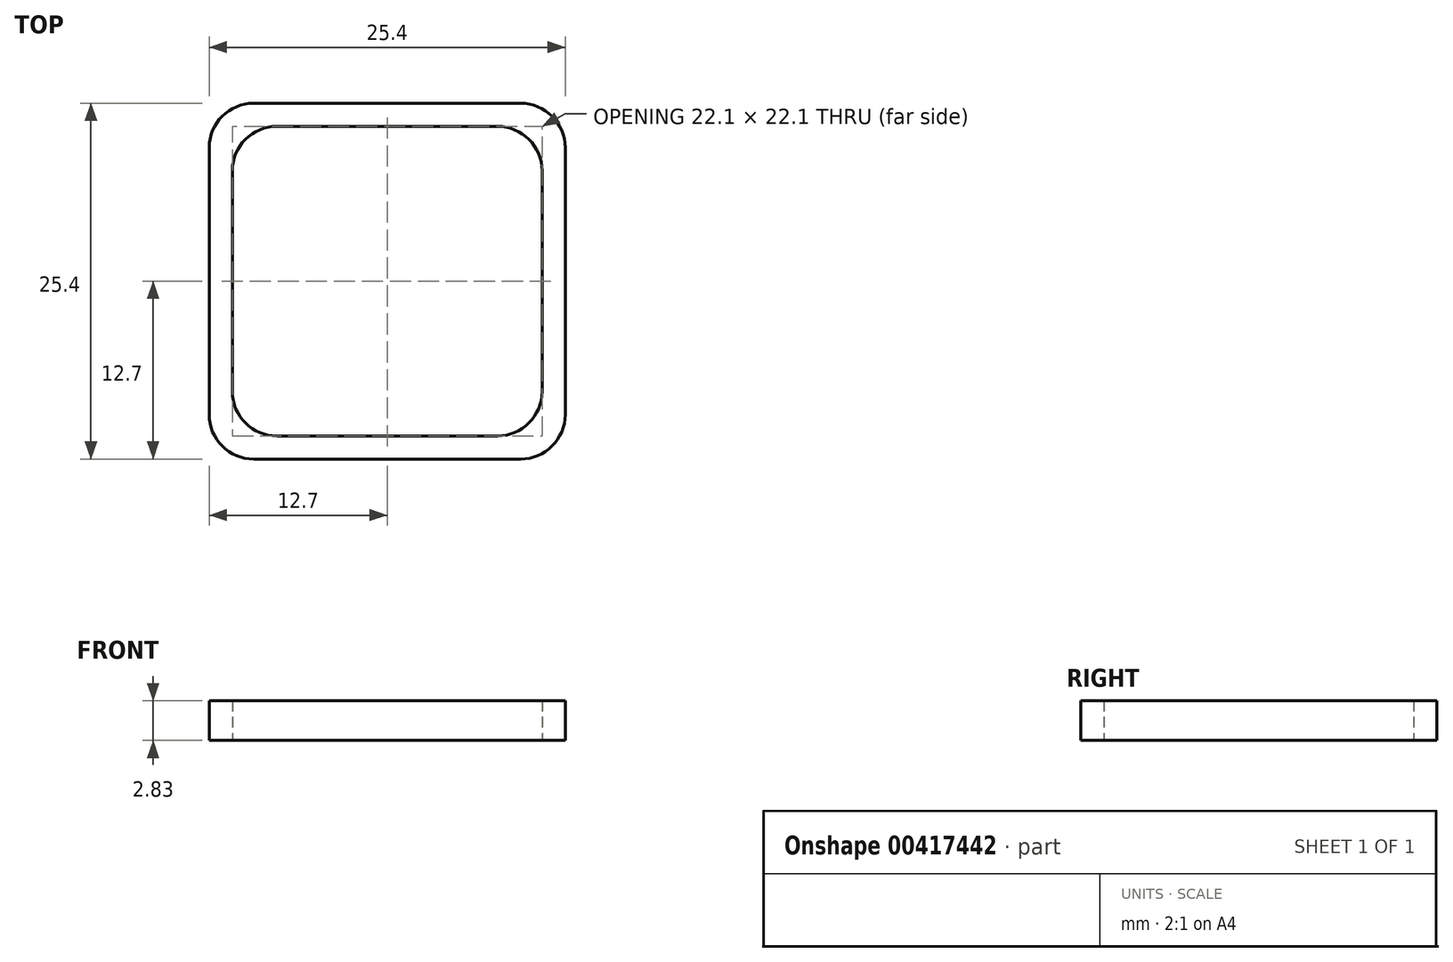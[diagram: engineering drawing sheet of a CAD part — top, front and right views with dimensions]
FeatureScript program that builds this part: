
annotation { "Feature Type Name" : "Feature", "Feature Type Description" : "" }
export const myFeature = defineFeature(function(context is Context, id is Id, definition is map)
    precondition{}
    {
        {
            assignVariable(context, id + "F0", {"name" : "BeamHeight", "anyValue" : 2.83});
        }
        {
            var Q0;
            Q0=qCreatedBy(makeId("Top.planeOp"),FACE);
            var sketch = newSketch(context, id + "F1", { "sketchPlane" : qUnion([Q0])});
            skPoint(sketch, "E0.middle", {"position": v(0, 0) * mm});
            skPoint(sketch, "E1.visualSharp", {"position": v(-12.7, 12.7) * mm});
            skPoint(sketch, "E2.visualSharp", {"position": v(12.7, 12.7) * mm});
            skPoint(sketch, "E3.visualSharp", {"position": v(12.7, -12.7) * mm});
            skPoint(sketch, "E4.visualSharp", {"position": v(-12.7, -12.7) * mm});
            skLineSegment(sketch, "E5.bottom", {"start": v(-7.87, 11.05) * mm, "end": v(7.87, 11.05) * mm});
            skLineSegment(sketch, "E5.top", {"start": v(-7.87, -11.05) * mm, "end": v(7.87, -11.05) * mm});
            skLineSegment(sketch, "E5.left", {"start": v(-11.05, 7.87) * mm, "end": v(-11.05, -7.87) * mm});
            skLineSegment(sketch, "E5.right", {"start": v(11.05, 7.87) * mm, "end": v(11.05, -7.87) * mm});
            skPoint(sketch, "E6.visualSharp", {"position": v(-11.05, 11.05) * mm});
            skArc(sketch, "E6.filletArc", {"start": v(-7.87, 11.05) * mm, "mid": v(-10.12, 10.12) * mm, "end": v(-11.05, 7.87) * mm});
            skPoint(sketch, "E7.visualSharp", {"position": v(11.05, 11.05) * mm});
            skArc(sketch, "E7.filletArc", {"start": v(11.05, 7.87) * mm, "mid": v(10.12, 10.12) * mm, "end": v(7.87, 11.05) * mm});
            skPoint(sketch, "E8.visualSharp", {"position": v(11.05, -11.05) * mm});
            skArc(sketch, "E8.filletArc", {"start": v(7.87, -11.05) * mm, "mid": v(10.12, -10.12) * mm, "end": v(11.05, -7.87) * mm});
            skPoint(sketch, "E9.visualSharp", {"position": v(-11.05, -11.05) * mm});
            skArc(sketch, "E9.filletArc", {"start": v(-11.05, -7.87) * mm, "mid": v(-10.12, -10.12) * mm, "end": v(-7.87, -11.05) * mm});
            skLineSegment(sketch, "E10.bottom", {"start": v(-12.7, 12.7) * mm, "end": v(12.7, 12.7) * mm});
            skLineSegment(sketch, "E10.top", {"start": v(-12.7, -12.7) * mm, "end": v(12.7, -12.7) * mm});
            skLineSegment(sketch, "E10.left", {"start": v(-12.7, 12.7) * mm, "end": v(-12.7, -12.7) * mm});
            skLineSegment(sketch, "E10.right", {"start": v(12.7, 12.7) * mm, "end": v(12.7, -12.7) * mm});
            skSolve(sketch);
        }
        {
            var Q0;
            Q0=makeQuery(id+"F1.imprint","IMPRINT",FACE,{"disambiguationData":[TD([[makeQuery(id+"F1.imprint","IMPRINT",EDGE,{"derivedFrom":sQuery(id+"F1.wireOp",EDGE,"E5.bottom")}),1.0]])]});
            extrude(context, id + "F2", {"entities" : qUnion([Q0]), "depth" : (getVariable(context, 'BeamHeight')) * mm});
        }
        {
            var Q0;
            Q0=makeQuery(id+"F2.opExtrude","SWEPT_FACE",FACE,{"disambiguationData":[OSD([sQuery(id+"F1.wireOp",EDGE,"E10.top")])]});
            var sketch = newSketch(context, id + "F3", { "sketchPlane" : qUnion([Q0])});
            skLineSegment(sketch, "E11", {"start": v(-12.7, 0) * mm, "end": v(12.7, 10.52) * mm});
            skLineSegment(sketch, "E12", {"start": v(12.7, 10.52) * mm, "end": v(12.7, 0) * mm});
            skLineSegment(sketch, "E13", {"start": v(12.7, 0) * mm, "end": v(-12.7, 0) * mm});
            skLineSegment(sketch, "E14", {"start": v(-12.7, 71.83) * mm, "end": v(12.7, 61.31) * mm});
            skLineSegment(sketch, "E15", {"start": v(12.7, 61.31) * mm, "end": v(12.7, 71.83) * mm});
            skLineSegment(sketch, "E16", {"start": v(12.7, 71.83) * mm, "end": v(-12.7, 71.83) * mm});
            skSolve(sketch);
        }
        {
            var Q0;
            Q0=makeQuery(id+"F3.imprint","IMPRINT",FACE,{"disambiguationData":[TD([[makeQuery(id+"F3.imprint","IMPRINT",EDGE,{"derivedFrom":sQuery(id+"F3.wireOp",EDGE,"E11")}),-1.0]])]});
            var Q1;
            Q1=makeQuery(id+"F3.imprint","IMPRINT",FACE,{"disambiguationData":[TD([[makeQuery(id+"F3.imprint","IMPRINT",EDGE,{"derivedFrom":sQuery(id+"F3.wireOp",EDGE,"tbfunD7k-3SZQ-cGiz-ijNi-D8s2jSZwsboX")}),1.0]])]});
            var Q2;
            Q2=makeQuery(id+"F3.imprint","IMPRINT",FACE,{"disambiguationData":[TD([[makeQuery(id+"F3.imprint","IMPRINT",EDGE,{"derivedFrom":sQuery(id+"F3.wireOp",EDGE,"E14")}),1.0]])]});
            extrude(context, id + "F4", {"entities" : qUnion([Q0, Q1, Q2]), "operationType" : NewBodyOperationType.REMOVE, "oppositeDirection" : true, "depth" : 25.4 * mm});
        }
        {
            var Q0;
            Q0=makeQuery(id+"F2.opExtrude","SWEPT_EDGE",EDGE,{"disambiguationData":[OSD([sQuery(id+"F1.wireOp",EDGE,"E10.bottom"),sQuery(id+"F1.wireOp",EDGE,"E10.left")])]});
            var Q1;
            Q1=makeQuery(id+"F2.opExtrude","SWEPT_EDGE",EDGE,{"disambiguationData":[OSD([sQuery(id+"F1.wireOp",EDGE,"E10.bottom"),sQuery(id+"F1.wireOp",EDGE,"E10.right")])]});
            var Q2;
            Q2=makeQuery(id+"F2.opExtrude","SWEPT_EDGE",EDGE,{"disambiguationData":[OSD([sQuery(id+"F1.wireOp",EDGE,"E10.top"),sQuery(id+"F1.wireOp",EDGE,"E10.left")])]});
            var Q3;
            Q3=makeQuery(id+"F2.opExtrude","SWEPT_EDGE",EDGE,{"disambiguationData":[OSD([sQuery(id+"F1.wireOp",EDGE,"E10.top"),sQuery(id+"F1.wireOp",EDGE,"E10.right")])]});
            fillet(context, id + "F5", {"entities" : qUnion([Q0, Q1, Q2, Q3]), "radius" : 3.17 * mm, "tangentPropagation" : true, "allowEdgeOverflow" : false});
        }
    });
